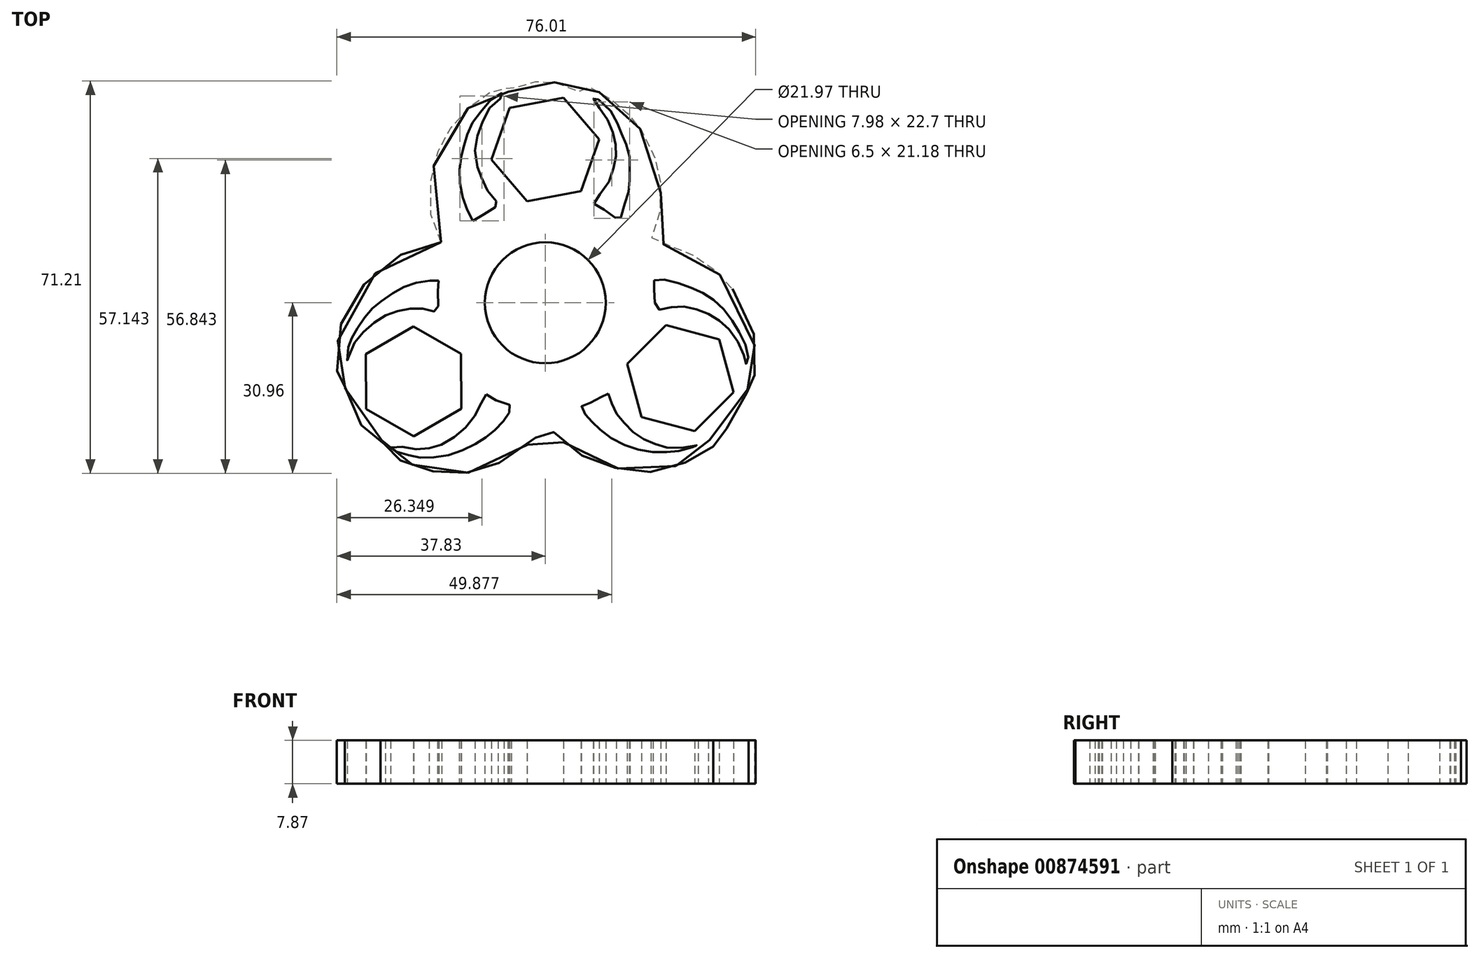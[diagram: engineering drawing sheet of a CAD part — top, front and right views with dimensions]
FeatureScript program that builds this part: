
annotation { "Feature Type Name" : "Feature", "Feature Type Description" : "" }
export const myFeature = defineFeature(function(context is Context, id is Id, definition is map)
    precondition{}
    {
        {
            var Q0;
            Q0=qCreatedBy(makeId("Top.planeOp"),FACE);
            var sketch = newSketch(context, id + "F0", { "sketchPlane" : qUnion([Q0])});
            skCircle(sketch, "E0", {"center": v(0, 0) * mm, "radius": 10.99 * mm});
            skSolve(sketch);
        }
        {
            var Q0;
            Q0=qCreatedBy(makeId("Top.planeOp"),FACE);
            var sketch = newSketch(context, id + "F1", { "sketchPlane" : qUnion([Q0])});
            skFitSpline(sketch, "E1", {"points": [v(-18.9, 10.99) * mm, v(-20.49, 15.25) * mm, v(-20.89, 21.24) * mm, v(-19.7, 26.84) * mm, v(-18.15, 30.1) * mm, v(-15.79, 33.59) * mm, v(-12.7, 36.35) * mm, v(-9.77, 38.38) * mm, v(-8.15, 39.28) * mm, v(-7.5, 38.87) * mm, v(-6.76, 38.3) * mm, v(-6.76, 38.4) * mm, v(-4.9, 39.23) * mm, v(-2.74, 39.95) * mm, v(-0.51, 40.25) * mm, v(1.8, 40) * mm, v(4.55, 39.23) * mm, v(7.16, 38.1) * mm, v(7.54, 39.15) * mm, v(10.07, 38.05) * mm, v(12.43, 36.58) * mm, v(14.37, 34.94) * mm, v(16.18, 32.91) * mm, v(18.07, 30.22) * mm, v(20.18, 25.45) * mm, v(20.87, 22.03) * mm, v(20.92, 17.8) * mm, v(20, 13.34) * mm, v(19.27, 11.06) * mm, v(22.3, 10.49) * mm, v(26.07, 9.06) * mm, v(28.91, 7.33) * mm, v(31.83, 4.92) * mm, v(34.72, 1.49) * mm, v(37.68, -4.53) * mm, v(38, -10.9) * mm, v(38, -13.12) * mm, v(36.88, -12.49) * mm, v(36.9, -14.16) * mm, v(36, -17.7) * mm, v(33.96, -21.47) * mm, v(31.17, -24.26) * mm, v(29.59, -25.24) * mm, v(30.5, -26.07) * mm, v(29.81, -26.45) * mm, v(27.33, -28.1) * mm, v(23.33, -29.77) * mm, v(20.69, -30.52) * mm, v(17.07, -30.75) * mm, v(14.35, -30.37) * mm, v(11.19, -29.54) * mm, v(8.47, -28.71) * mm, v(5.08, -26.68) * mm, v(2.6, -24.64) * mm, v(0.7, -22.53) * mm, v(0, -22.08) * mm, v(-1.33, -23.96) * mm, v(-4.35, -26.6) * mm, v(-9.02, -29.4) * mm, v(-12.04, -30.3) * mm, v(-14.38, -30.9) * mm, v(-17.24, -30.9) * mm, v(-20.1, -30.67) * mm, v(-22.98, -29.77) * mm, v(-25.92, -28.79) * mm, v(-28.18, -27.66) * mm, v(-29.91, -26.37) * mm, v(-29, -25.4) * mm, v(-30.67, -24.72) * mm, v(-33.3, -22.3) * mm, v(-35.5, -18.76) * mm, v(-36.4, -14.38) * mm, v(-36.55, -12.72) * mm, v(-37.46, -13.18) * mm, v(-37.83, -11) * mm, v(-37.38, -5.1) * mm, v(-35.38, 0) * mm, v(-31.97, 4.24) * mm, v(-27.48, 7.96) * mm, v(-23.07, 9.9) * mm, v(-18.9, 10.99) * mm]});
            skFitSpline(sketch, "E2", {"points": [v(-19.35, 4) * mm, v(-19.59, 1.46) * mm, v(-19.59, -1.49) * mm, v(-21.21, -1.25) * mm, v(-24.15, -1.02) * mm, v(-27.25, -1.64) * mm, v(-30.27, -3.03) * mm, v(-33.29, -5.59) * mm, v(-35.3, -8.68) * mm, v(-35.92, -10.7) * mm, v(-35.76, -8.14) * mm, v(-35.14, -6.44) * mm, v(-33.75, -4.12) * mm, v(-31.9, -1.56) * mm, v(-30.19, 0) * mm, v(-27.1, 2.07) * mm, v(-24.3, 3.4) * mm, v(-20.82, 4) * mm, v(-19.35, 4) * mm]});
            skFitSpline(sketch, "E3", {"points": [v(19.73, 4.09) * mm, v(19.81, 1.84) * mm, v(20.28, -1.1) * mm, v(23.14, -0.79) * mm, v(26.78, -1.02) * mm, v(30.34, -2.41) * mm, v(33.28, -4.81) * mm, v(35.91, -9.15) * mm, v(36.45, -11.08) * mm, v(36.84, -9.92) * mm, v(35.6, -6.05) * mm, v(33.36, -2.41) * mm, v(30.26, 0.76) * mm, v(26.85, 2.54) * mm, v(22.83, 3.93) * mm, v(19.73, 4.09) * mm]});
            skFitSpline(sketch, "E4", {"points": [v(-10.71, -16.65) * mm, v(-8.77, -17.78) * mm, v(-6.18, -18.8) * mm, v(-6.66, -20.15) * mm, v(-7.8, -21.77) * mm, v(-9.63, -23.5) * mm, v(-11.36, -24.85) * mm, v(-14.16, -26.41) * mm, v(-17.62, -27.65) * mm, v(-21.18, -28.14) * mm, v(-23.87, -27.92) * mm, v(-26.2, -27.27) * mm, v(-28.08, -26.57) * mm, v(-27.54, -26.03) * mm, v(-24.52, -26.52) * mm, v(-21.55, -26.46) * mm, v(-18.86, -25.76) * mm, v(-15.62, -23.71) * mm, v(-13.25, -21.18) * mm, v(-11.52, -18) * mm, v(-10.71, -16.65) * mm]});
            skFitSpline(sketch, "E5", {"points": [v(11.44, -16.48) * mm, v(12.16, -18.63) * mm, v(13.46, -20.82) * mm, v(15.51, -23.1) * mm, v(18.02, -24.85) * mm, v(20.83, -25.96) * mm, v(24.28, -26.37) * mm, v(27.72, -25.87) * mm, v(25.35, -26.63) * mm, v(22.3, -27.13) * mm, v(18.46, -27) * mm, v(14.48, -25.87) * mm, v(10.77, -23.73) * mm, v(8.76, -21.9) * mm, v(7.33, -20.33) * mm, v(6.57, -18.85) * mm, v(8.05, -18.18) * mm, v(10.46, -16.89) * mm, v(11.44, -16.48) * mm]});
            skFitSpline(sketch, "E6", {"points": [v(8.8, 18) * mm, v(11.76, 16.3) * mm, v(13.36, 15.02) * mm, v(14.37, 17.76) * mm, v(15.24, 20.74) * mm, v(15.24, 23.66) * mm, v(15.3, 26.33) * mm, v(14.37, 29.5) * mm, v(13.42, 31.74) * mm, v(11.76, 34.94) * mm, v(8.74, 37.34) * mm, v(8.98, 36.58) * mm, v(11.05, 33.63) * mm, v(12.43, 30.22) * mm, v(12.87, 27.37) * mm, v(12.43, 24.57) * mm, v(10.6, 20.5) * mm, v(8.8, 18) * mm]});
            skFitSpline(sketch, "E7", {"points": [v(-13.13, 14.83) * mm, v(-10.87, 16.28) * mm, v(-8.92, 17.47) * mm, v(-8.6, 18.04) * mm, v(-9.8, 19.3) * mm, v(-11.36, 22.31) * mm, v(-12.07, 23.82) * mm, v(-12.76, 27.53) * mm, v(-12.2, 30.8) * mm, v(-10.8, 34.13) * mm, v(-8.92, 36.58) * mm, v(-7.48, 37.6) * mm, v(-8.23, 38.05) * mm, v(-10.75, 35.77) * mm, v(-12.7, 33.5) * mm, v(-13.95, 31.18) * mm, v(-14.58, 29.23) * mm, v(-15.02, 27.66) * mm, v(-15.46, 25.4) * mm, v(-15.59, 22.63) * mm, v(-15.08, 19.42) * mm, v(-14.2, 16.97) * mm, v(-13.13, 14.83) * mm]});
            skSolve(sketch);
        }
        {
            var Q0;
            Q0=makeQuery(id+"F1.imprint","IMPRINT",FACE,{"disambiguationData":[TD([[makeQuery(id+"F1.imprint","IMPRINT",EDGE,{"derivedFrom":sQuery(id+"F1.wireOp",EDGE,"E1")}),-1.0]])]});
            extrude(context, id + "F2", {"entities" : qUnion([Q0]), "depth" : 7.87 * mm, "offsetDistance" : 25.4 * mm});
        }
        {
            var Q0;
            Q0=qCreatedBy(makeId("Top.planeOp"),FACE);
            var sketch = newSketch(context, id + "F3", { "sketchPlane" : qUnion([Q0])});
            skCircle(sketch, "E8.cCircle", {"center": v(0, 27.82) * mm, "radius": 8.64 * mm, "construction": true});
            skLineSegment(sketch, "E8.0", {"start": v(9.8, 29.68) * mm, "end": v(6.5, 20.27) * mm});
            skLineSegment(sketch, "E8.1", {"start": v(6.5, 20.27) * mm, "end": v(-3.3, 18.41) * mm});
            skLineSegment(sketch, "E8.2", {"start": v(-3.3, 18.41) * mm, "end": v(-9.8, 25.97) * mm});
            skLineSegment(sketch, "E8.3", {"start": v(-9.8, 25.97) * mm, "end": v(-6.5, 35.38) * mm});
            skLineSegment(sketch, "E8.4", {"start": v(-6.5, 35.38) * mm, "end": v(3.3, 37.24) * mm});
            skLineSegment(sketch, "E8.5", {"start": v(3.3, 37.24) * mm, "end": v(9.8, 29.68) * mm});
            skPoint(sketch, "E8.0.midPoint", {"position": v(8.15, 24.97) * mm});
            skCircle(sketch, "E9.cCircle", {"center": v(-23.91, -14.29) * mm, "radius": 8.64 * mm, "construction": true});
            skLineSegment(sketch, "E9.0", {"start": v(-15.26, -19.24) * mm, "end": v(-23.87, -24.26) * mm});
            skLineSegment(sketch, "E9.1", {"start": v(-23.87, -24.26) * mm, "end": v(-32.53, -19.31) * mm});
            skLineSegment(sketch, "E9.2", {"start": v(-32.53, -19.31) * mm, "end": v(-32.57, -9.34) * mm});
            skLineSegment(sketch, "E9.3", {"start": v(-32.57, -9.34) * mm, "end": v(-23.96, -4.32) * mm});
            skLineSegment(sketch, "E9.4", {"start": v(-23.96, -4.32) * mm, "end": v(-15.3, -9.26) * mm});
            skLineSegment(sketch, "E9.5", {"start": v(-15.3, -9.26) * mm, "end": v(-15.26, -19.24) * mm});
            skPoint(sketch, "E9.0.midPoint", {"position": v(-19.56, -21.75) * mm});
            skCircle(sketch, "E10.cCircle", {"center": v(24.51, -13.69) * mm, "radius": 8.64 * mm, "construction": true});
            skLineSegment(sketch, "E10.0", {"start": v(34.15, -16.27) * mm, "end": v(27.1, -23.32) * mm});
            skLineSegment(sketch, "E10.1", {"start": v(27.1, -23.32) * mm, "end": v(17.46, -20.73) * mm});
            skLineSegment(sketch, "E10.2", {"start": v(17.46, -20.73) * mm, "end": v(14.88, -11.1) * mm});
            skLineSegment(sketch, "E10.3", {"start": v(14.88, -11.1) * mm, "end": v(21.94, -4.05) * mm});
            skLineSegment(sketch, "E10.4", {"start": v(21.94, -4.05) * mm, "end": v(31.57, -6.64) * mm});
            skLineSegment(sketch, "E10.5", {"start": v(31.57, -6.64) * mm, "end": v(34.15, -16.27) * mm});
            skPoint(sketch, "E10.0.midPoint", {"position": v(30.62, -19.8) * mm});
            skSolve(sketch);
        }
        {
            var Q0;
            Q0 = qSketchRegion(id + "F0", true);
            extrude(context, id + "F4", {"entities" : qUnion([Q0]), "operationType" : NewBodyOperationType.REMOVE, "depth" : 49.53 * mm, "offsetDistance" : 25.4 * mm});
        }
        {
            var Q0;
            Q0 = qSketchRegion(id + "F3", true);
            extrude(context, id + "F5", {"entities" : qUnion([Q0]), "operationType" : NewBodyOperationType.REMOVE, "depth" : 41.4 * mm, "offsetDistance" : 25.4 * mm});
        }
    });
